# Revit family: ProTilt® High Performance AW-CA Window-SG & DG- Side Lite
name_source: partatom
category: Windows
units: mm (PartAtom-declared; Revit-internal decimal feet)

## family parameters
Always vertical = Yes
Cut with Voids When Loaded = No
Host = Wall
OmniClass Number = 23.30.20.00
OmniClass Title = Windows
Room Calculation Point = No
Shared = No

## types (1)
- ASW100 MITRED ADAPTOR
    Analytic Construction = <None>
    Default Sill Height = 999 mm  [stored 3.27756 ft]
    Define Thermal Properties by = Schematic Type
    Ext Frame Width = 49.4 mm
    Height = 0 mm  [stored 0 ft]
    Manufacturer = ALSPEC
    Model = ProTilt® High Performance Awning/Casement Window-SG & DG
    Offset = 10 mm  [stored 0.0328084 ft]
    Rough Height = 0 mm  [stored 0 ft]
    Rough Width = 0 mm  [stored 0 ft]
    TOLERANCE = 0 mm  [stored 0 ft]
    URL = WWW.ALSPEC.COM.AU
    Wall Closure = By host
    Width = 0 mm  [stored 0 ft]
    YEAR = 2022

note: [stored X ft] marks values corroborated as IEEE doubles in the binary element streams (Revit-internal decimal feet)

## geometry (parser evidence)
native form markers: Sweep x17
no freeform markers — native parametric forms only
